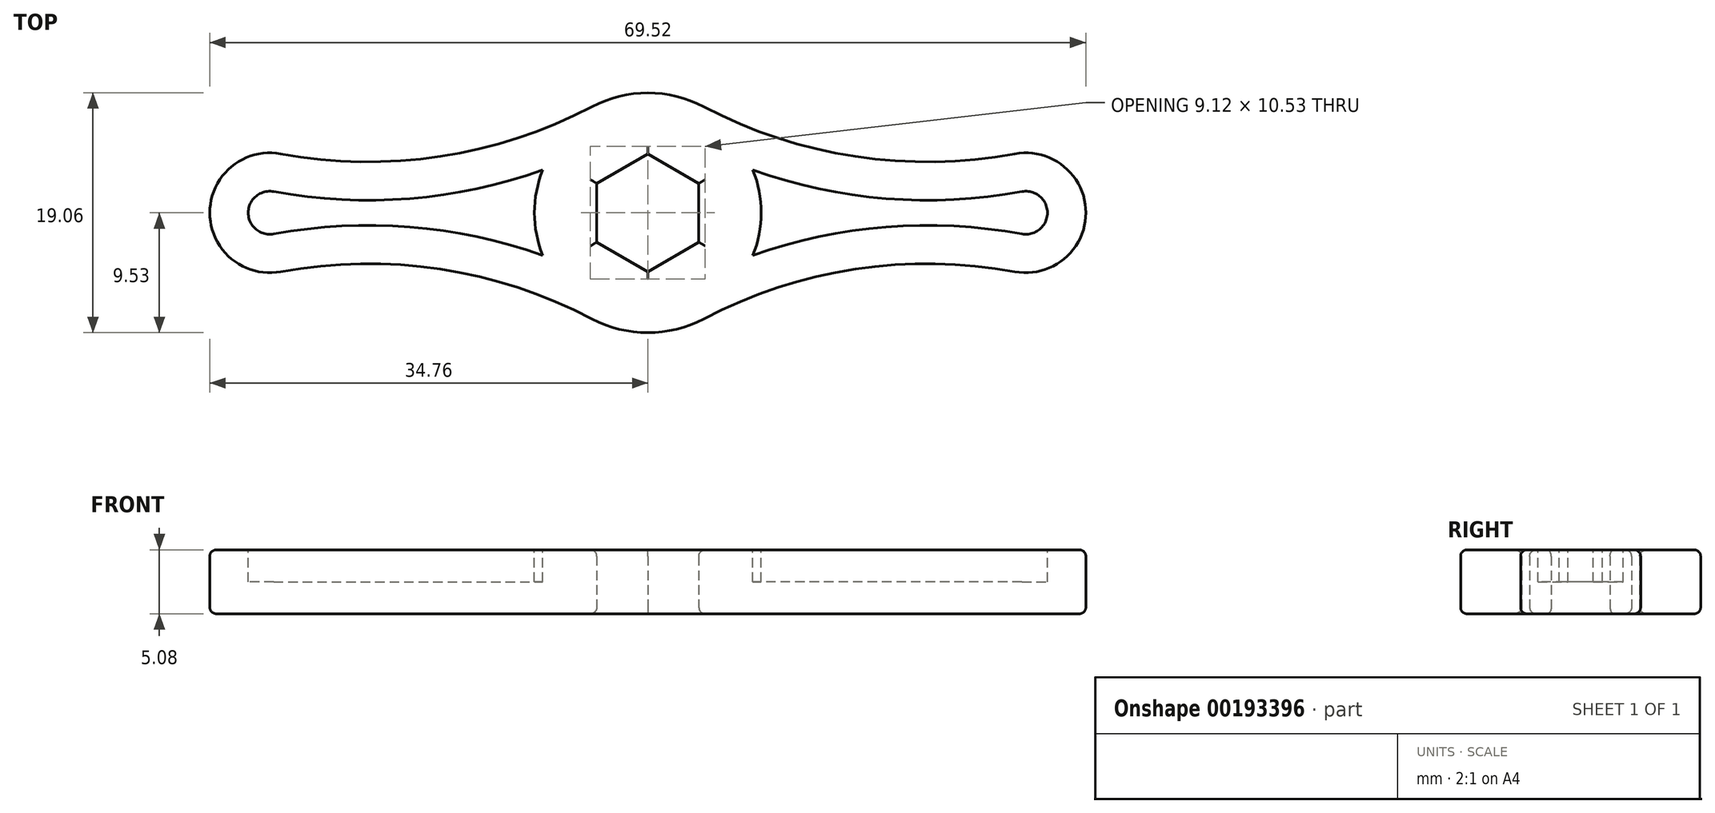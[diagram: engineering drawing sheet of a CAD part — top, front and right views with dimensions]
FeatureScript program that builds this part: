
annotation { "Feature Type Name" : "Feature", "Feature Type Description" : "" }
export const myFeature = defineFeature(function(context is Context, id is Id, definition is map)
    precondition{}
    {
        {
            var Q0;
            Q0=qCreatedBy(makeId("Top.planeOp"),FACE);
            var sketch = newSketch(context, id + "F0", { "sketchPlane" : qUnion([Q0])});
            skLineSegment(sketch, "E0", {"start": v(0, 0) * mm, "end": v(-30, 0) * mm, "construction": true});
            skArc(sketch, "E1", {"start": v(-4.44, -8.43) * mm, "mid": v(-2.28, -9.25) * mm, "end": v(0, -9.53) * mm});
            skArc(sketch, "E2", {"start": v(-4.44, -8.43) * mm, "mid": v(-16.47, -4.47) * mm, "end": v(-29.13, -4.68) * mm});
            skArc(sketch, "E3", {"start": v(-29.13, 4.68) * mm, "mid": v(-34.76, 0) * mm, "end": v(-29.13, -4.68) * mm});
            skArc(sketch, "E4.MirrorCS", {"start": v(-4.44, 8.43) * mm, "mid": v(-16.47, 4.47) * mm, "end": v(-29.13, 4.68) * mm});
            skLineSegment(sketch, "E5", {"start": v(0, -14.56) * mm, "end": v(0, 14.09) * mm, "construction": true});
            skArc(sketch, "E6.trimOffspring", {"start": v(0, 9.53) * mm, "mid": v(-2.28, 9.25) * mm, "end": v(-4.44, 8.43) * mm});
            skArc(sketch, "E7.MirrorCS", {"start": v(4.44, -8.43) * mm, "mid": v(2.28, -9.25) * mm, "end": v(0, -9.53) * mm});
            skArc(sketch, "E8.MirrorCS", {"start": v(0, 9.53) * mm, "mid": v(2.28, 9.25) * mm, "end": v(4.44, 8.43) * mm});
            skLineSegment(sketch, "E9.MirrorCS", {"start": v(0, 0) * mm, "end": v(30, 0) * mm, "construction": true});
            skArc(sketch, "E10.MirrorCS", {"start": v(4.44, -8.43) * mm, "mid": v(16.47, -4.47) * mm, "end": v(29.13, -4.68) * mm});
            skArc(sketch, "E11.MirrorCS", {"start": v(29.13, 4.68) * mm, "mid": v(34.76, 0) * mm, "end": v(29.13, -4.68) * mm});
            skArc(sketch, "E12.MirrorCS", {"start": v(4.44, 8.43) * mm, "mid": v(16.47, 4.47) * mm, "end": v(29.13, 4.68) * mm});
            skCircle(sketch, "E13.cCircle", {"center": v(0, 0) * mm, "radius": 4.05 * mm, "construction": true});
            skLineSegment(sketch, "E13.0", {"start": v(0, 4.68) * mm, "end": v(4.05, 2.34) * mm});
            skLineSegment(sketch, "E13.1", {"start": v(4.05, 2.34) * mm, "end": v(4.05, -2.34) * mm});
            skLineSegment(sketch, "E13.2", {"start": v(4.05, -2.34) * mm, "end": v(0, -4.68) * mm});
            skLineSegment(sketch, "E13.3", {"start": v(0, -4.68) * mm, "end": v(-4.05, -2.34) * mm});
            skLineSegment(sketch, "E13.4", {"start": v(-4.05, -2.34) * mm, "end": v(-4.05, 2.34) * mm});
            skLineSegment(sketch, "E13.5", {"start": v(-4.05, 2.34) * mm, "end": v(0, 4.68) * mm});
            skPoint(sketch, "E13.0.midPoint", {"position": v(2.03, 3.5) * mm});
            skSolve(sketch);
        }
        {
            var Q0;
            Q0=makeQuery(id+"F0.imprint","IMPRINT",FACE,{"disambiguationData":[TD([[makeQuery(id+"F0.imprint","IMPRINT",EDGE,{"derivedFrom":sQuery(id+"F0.wireOp",EDGE,"E1")}),1.0]])]});
            extrude(context, id + "F1", {"entities" : qUnion([Q0]), "depth" : 5.08 * mm});
        }
        {
            var Q0;
            Q0=makeQuery(id+"F1.opExtrude","CAP_FACE",FACE,{"disambiguationData":[OSD([sQuery(id+"F0.wireOp",EDGE,"E1"),sQuery(id+"F0.wireOp",EDGE,"E2"),sQuery(id+"F0.wireOp",EDGE,"E3"),sQuery(id+"F0.wireOp",EDGE,"E4.MirrorCS"),sQuery(id+"F0.wireOp",EDGE,"E6.trimOffspring"),sQuery(id+"F0.wireOp",EDGE,"E7.MirrorCS"),sQuery(id+"F0.wireOp",EDGE,"E8.MirrorCS"),sQuery(id+"F0.wireOp",EDGE,"E10.MirrorCS"),sQuery(id+"F0.wireOp",EDGE,"E11.MirrorCS"),sQuery(id+"F0.wireOp",EDGE,"E12.MirrorCS"),sQuery(id+"F0.wireOp",EDGE,"E13.0"),sQuery(id+"F0.wireOp",EDGE,"E13.1"),sQuery(id+"F0.wireOp",EDGE,"E13.2"),sQuery(id+"F0.wireOp",EDGE,"E13.3"),sQuery(id+"F0.wireOp",EDGE,"E13.4"),sQuery(id+"F0.wireOp",EDGE,"E13.5")])],"isStart":false});
            fillet(context, id + "F2", {"entities" : qUnion([Q0]), "radius" : 0.5 * mm, "tangentPropagation" : true, "allowEdgeOverflow" : false});
        }
        {
            var Q0;
            Q0=makeQuery(id+"F1.opExtrude","CAP_FACE",FACE,{"disambiguationData":[OSD([sQuery(id+"F0.wireOp",EDGE,"E1"),sQuery(id+"F0.wireOp",EDGE,"E2"),sQuery(id+"F0.wireOp",EDGE,"E3"),sQuery(id+"F0.wireOp",EDGE,"E4.MirrorCS"),sQuery(id+"F0.wireOp",EDGE,"E6.trimOffspring"),sQuery(id+"F0.wireOp",EDGE,"E7.MirrorCS"),sQuery(id+"F0.wireOp",EDGE,"E8.MirrorCS"),sQuery(id+"F0.wireOp",EDGE,"E10.MirrorCS"),sQuery(id+"F0.wireOp",EDGE,"E11.MirrorCS"),sQuery(id+"F0.wireOp",EDGE,"E12.MirrorCS"),sQuery(id+"F0.wireOp",EDGE,"E13.0"),sQuery(id+"F0.wireOp",EDGE,"E13.1"),sQuery(id+"F0.wireOp",EDGE,"E13.2"),sQuery(id+"F0.wireOp",EDGE,"E13.3"),sQuery(id+"F0.wireOp",EDGE,"E13.4"),sQuery(id+"F0.wireOp",EDGE,"E13.5")])],"isStart":true});
            fillet(context, id + "F3", {"entities" : qUnion([Q0]), "radius" : 0.5 * mm, "tangentPropagation" : true, "allowEdgeOverflow" : false});
        }
        {
            var Q0;
            Q0=makeQuery(id+"F1.opExtrude","CAP_FACE",FACE,{"disambiguationData":[OSD([sQuery(id+"F0.wireOp",EDGE,"E1"),sQuery(id+"F0.wireOp",EDGE,"E2"),sQuery(id+"F0.wireOp",EDGE,"E3"),sQuery(id+"F0.wireOp",EDGE,"E4.MirrorCS"),sQuery(id+"F0.wireOp",EDGE,"E6.trimOffspring"),sQuery(id+"F0.wireOp",EDGE,"E7.MirrorCS"),sQuery(id+"F0.wireOp",EDGE,"E8.MirrorCS"),sQuery(id+"F0.wireOp",EDGE,"E10.MirrorCS"),sQuery(id+"F0.wireOp",EDGE,"E11.MirrorCS"),sQuery(id+"F0.wireOp",EDGE,"E12.MirrorCS"),sQuery(id+"F0.wireOp",EDGE,"E13.0"),sQuery(id+"F0.wireOp",EDGE,"E13.1"),sQuery(id+"F0.wireOp",EDGE,"E13.2"),sQuery(id+"F0.wireOp",EDGE,"E13.3"),sQuery(id+"F0.wireOp",EDGE,"E13.4"),sQuery(id+"F0.wireOp",EDGE,"E13.5")])],"isStart":false});
            var sketch = newSketch(context, id + "F4", { "sketchPlane" : qUnion([Q0])});
            skArc(sketch, "E14.0", {"start": v(29.69, 1.69) * mm, "mid": v(18.9, 1.13) * mm, "end": v(8.33, 3.4) * mm});
            skArc(sketch, "E15.0", {"start": v(8.33, -3.4) * mm, "mid": v(18.9, -1.13) * mm, "end": v(29.69, -1.69) * mm});
            skArc(sketch, "E16", {"start": v(29.69, -1.69) * mm, "mid": v(31.71, 0) * mm, "end": v(29.69, 1.69) * mm});
            skArc(sketch, "E17.0", {"start": v(-8.33, 3.4) * mm, "mid": v(-18.9, 1.13) * mm, "end": v(-29.69, 1.69) * mm});
            skArc(sketch, "E18.0", {"start": v(-29.69, -1.69) * mm, "mid": v(-18.9, -1.13) * mm, "end": v(-8.33, -3.4) * mm});
            skArc(sketch, "E19", {"start": v(-29.69, 1.69) * mm, "mid": v(-31.71, 0) * mm, "end": v(-29.69, -1.69) * mm});
            skArc(sketch, "E20", {"start": v(-8.33, 3.4) * mm, "mid": v(-9, 0) * mm, "end": v(-8.33, -3.4) * mm});
            skArc(sketch, "E21.trimOffspring", {"start": v(8.33, -3.4) * mm, "mid": v(9, 0) * mm, "end": v(8.33, 3.4) * mm});
            skSolve(sketch);
        }
        {
            var Q0;
            Q0 = qSketchRegion(id + "F4", true);
            extrude(context, id + "F5", {"entities" : qUnion([Q0]), "operationType" : NewBodyOperationType.REMOVE, "oppositeDirection" : true, "depth" : 2.54 * mm});
        }
    });
